# Revit family: Sanitary_Accessories_DURAVIT-AG_Starck-T-Towel-hooks-60x76x50-mm-009930
name_source: partatom
category: Generic Models
revit_build: Autodesk Revit 2018 (Build: 20180329_1100(x64)
units: mm (PartAtom-declared; Revit-internal decimal feet)

## family parameters
Can host rebar = No
Cut with Voids When Loaded = No
Host = Face
OmniClass Number = 23.31.25.25
OmniClass Title = Towel Bars
Part Type = Normal
Room Calculation Point = No
Round Connector Dimension = Use Diameter
Shared = No

## types (2) — shared parameters
BIMobject category = Bathroom Accessories
Default Elevation = 1219 mm
Design country = Germany
ETIM classification = EC010552 | Towel hook
Edition number = 1
IFC Classification = Furnishing Element
Installation instructions = https://pro.duravit.com
Manufacturer = Duravit
Manufacturer country = Germany
Manufacturer name = DURAVIT AG
Masterformat 2014 Code = 10 28 00
Masterformat 2014 Description = Toilet, Bath, and Laundry Accessories
Material main = Brass
Model = Starck T Towel hooks 60x76x50 mm - 009930
OmniClass Code = 23-31 25 25
OmniClass Description = Towel Bars
Product Guid = 2ad82fdf-49b9-42db-8449-8414a86717d7
Product SKU = Starck-T-Towel-hooks-60x76x50-mm-009930
Product certification = https://pro.duravit.com
Product data url = https://bimobject.com
Product family = Starck T
Product group = Towel hook
Product name = Starck T Towel hooks 60x76x50 mm - 009930
Product url = https://pro.duravit.com
QR code = https://bimobject.com
Technical description = https://pro.duravit.com
UNSPSC Code = 301815
URL = https://www.duravit.com
Uniclass 2015 Code = Pr_40_20_76_90
Uniclass 2015 Name = Towel rails
Uniformat II Code = E2010
Uniformat II Description = Fixed Furnishings
Weight Net (Kg) = 0.21
Youtube clip = https://pro.duravit.com

## per-type parameters (varying)
| type | Description | Main material |
| 10 - Chrome | Duravit Starck T Towel hooks Chrome 60x76x50 mm - 0099301000 | Duravit - Metal - 10 - Chrome |
| 46 - Black Matt | Duravit Starck T Towel hooks Black Matt 60x76x50 mm - 0099304600 | Duravit - Metal - 46 - Black Matt |

## geometry (parser evidence)
native form markers: Sweep x4
no freeform markers — native parametric forms only
